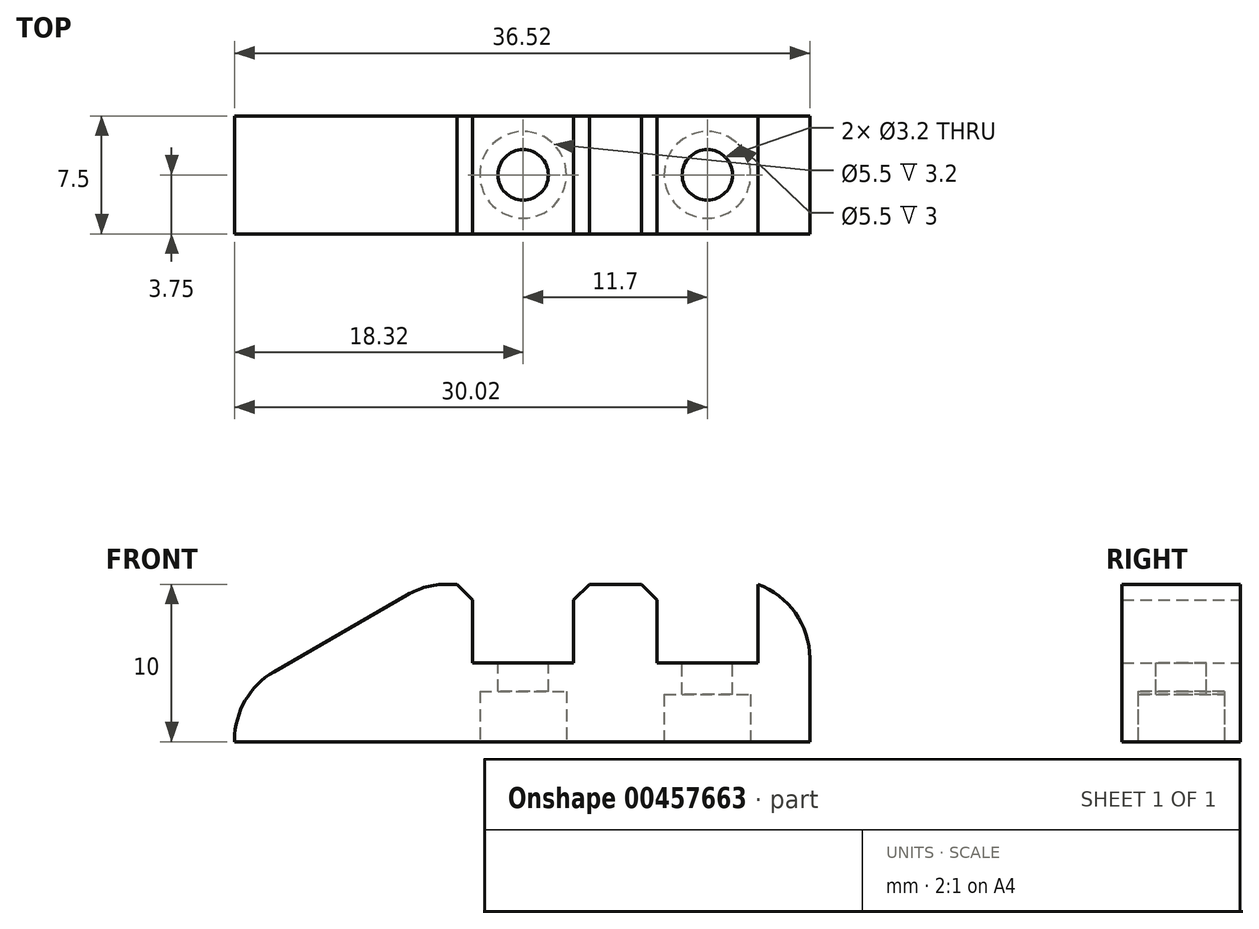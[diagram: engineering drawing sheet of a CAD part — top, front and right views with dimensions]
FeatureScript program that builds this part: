
annotation { "Feature Type Name" : "Feature", "Feature Type Description" : "" }
export const myFeature = defineFeature(function(context is Context, id is Id, definition is map)
    precondition{}
    {
        {
            var Q0;
            Q0=qCreatedBy(makeId("Front.planeOp"),FACE);
            var sketch = newSketch(context, id + "F0", { "sketchPlane" : qUnion([Q0])});
            skLineSegment(sketch, "E0", {"start": v(0, 0) * mm, "end": v(0, 10) * mm});
            skLineSegment(sketch, "E1", {"start": v(0, 10) * mm, "end": v(-3, 10) * mm});
            skLineSegment(sketch, "E2", {"start": v(-3, 10) * mm, "end": v(-3, 5) * mm});
            skLineSegment(sketch, "E3", {"start": v(-3, 5) * mm, "end": v(-9.4, 5) * mm});
            skLineSegment(sketch, "E4", {"start": v(-9.4, 5) * mm, "end": v(-9.4, 10) * mm});
            skLineSegment(sketch, "E5", {"start": v(-9.4, 10) * mm, "end": v(-12.4, 10) * mm});
            skLineSegment(sketch, "E6", {"start": v(-12.4, 10) * mm, "end": v(-24.52, 3) * mm});
            skLineSegment(sketch, "E7", {"start": v(-24.52, 3) * mm, "end": v(-24.52, 0) * mm});
            skLineSegment(sketch, "E8", {"start": v(-24.52, 0) * mm, "end": v(0, 0) * mm});
            skSolve(sketch);
        }
        {
            var Q0;
            Q0=makeQuery(id+"F0.imprint","IMPRINT",FACE,{"disambiguationData":[TD([[makeQuery(id+"F0.imprint","IMPRINT",EDGE,{"derivedFrom":sQuery(id+"F0.wireOp",EDGE,"E0")}),1.0]])]});
            extrude(context, id + "F1", {"entities" : qUnion([Q0]), "depth" : 7.5 * mm});
        }
        {
            var Q0;
            Q0=makeQuery(id+"F1.opExtrude","SWEPT_FACE",FACE,{"disambiguationData":[OSD([sQuery(id+"F0.wireOp",EDGE,"E3")])]});
            var sketch = newSketch(context, id + "F2", { "sketchPlane" : qUnion([Q0])});
            skCircle(sketch, "E9", {"center": v(-6.2, -3.75) * mm, "radius": 1.6 * mm});
            skSolve(sketch);
        }
        {
            var Q0;
            Q0=makeQuery(id+"F2.imprint","IMPRINT",FACE,{"disambiguationData":[TD([[makeQuery(id+"F2.imprint","IMPRINT",EDGE,{"derivedFrom":sQuery(id+"F2.wireOp",EDGE,"E9")}),1.0]])]});
            extrude(context, id + "F3", {"entities" : qUnion([Q0]), "operationType" : NewBodyOperationType.REMOVE, "endBound" : BoundingType.THROUGH_ALL, "oppositeDirection" : true, "depth" : 25 * mm});
        }
        {
            var Q0;
            Q0=makeQuery(id+"F1.opExtrude","SWEPT_FACE",FACE,{"disambiguationData":[OSD([sQuery(id+"F0.wireOp",EDGE,"E8")])]});
            var sketch = newSketch(context, id + "F4", { "sketchPlane" : qUnion([Q0])});
            skCircle(sketch, "E10", {"center": v(-6.2, 3.75) * mm, "radius": 2.75 * mm});
            skSolve(sketch);
        }
        {
            var Q0;
            Q0=makeQuery(id+"F4.imprint","IMPRINT",FACE,{"disambiguationData":[TD([[makeQuery(id+"F4.imprint","IMPRINT",EDGE,{"derivedFrom":sQuery(id+"F4.wireOp",EDGE,"E10")}),1.0]])]});
            extrude(context, id + "F5", {"entities" : qUnion([Q0]), "operationType" : NewBodyOperationType.REMOVE, "oppositeDirection" : true, "depth" : 3.2 * mm});
        }
        {
            var Q0;
            Q0=makeQuery(id+"F1.opExtrude","SWEPT_EDGE",EDGE,{"disambiguationData":[OSD([sQuery(id+"F0.wireOp",EDGE,"E5"),sQuery(id+"F0.wireOp",EDGE,"E6")])]});
            var Q1;
            Q1=makeQuery(id+"F1.opExtrude","SWEPT_EDGE",EDGE,{"disambiguationData":[OSD([sQuery(id+"F0.wireOp",EDGE,"E6"),sQuery(id+"F0.wireOp",EDGE,"E7")])]});
            fillet(context, id + "F6", {"entities" : qUnion([Q0, Q1]), "radius" : 5 * mm, "tangentPropagation" : true, "allowEdgeOverflow" : false});
        }
        {
            var Q0;
            Q0=makeQuery(id+"F2dZ7Sqy7HbEyPQ_1.opFillet","BLEND_EDGE",EDGE,{"blendedFrom":[makeQuery(id+"F1.opExtrude","SWEPT_EDGE",EDGE,{"disambiguationData":[OSD([sQuery(id+"F0.wireOp",EDGE,"E0"),sQuery(id+"F0.wireOp",EDGE,"E1")])]}),makeQuery(id+"F1.opExtrude","SWEPT_FACE",FACE,{"disambiguationData":[OSD([sQuery(id+"F0.wireOp",EDGE,"E2")])]})],"blendedInto":[makeQuery(id+"F1.opExtrude","SWEPT_FACE",FACE,{"disambiguationData":[OSD([sQuery(id+"F0.wireOp",EDGE,"E2")])]})]});
            var Q1;
            Q1=makeQuery(id+"F1.opExtrude","SWEPT_EDGE",EDGE,{"disambiguationData":[OSD([sQuery(id+"F0.wireOp",EDGE,"E4"),sQuery(id+"F0.wireOp",EDGE,"E5")])]});
            chamfer(context, id + "F7", {"entities" : qUnion([Q0, Q1]), "width" : 1 * mm, "tangentPropagation" : true});
        }
        {
            var Q0;
            Q0=makeQuery(id+"F1.opExtrude","SWEPT_FACE",FACE,{"disambiguationData":[OSD([sQuery(id+"F0.wireOp",EDGE,"E0")])]});
            extrude(context, id + "F8", {"entities" : qUnion([Q0]), "operationType" : NewBodyOperationType.ADD, "depth" : 12 * mm});
        }
        {
            var Q0;
            {var subQ0=sQuery(id+"F0.wireOp",EDGE,"E0");Q0=makeQuery(id+"F8.boolean.opBoolean","MERGE",FACE,{"derivedFrom":[makeQuery(id+"F1.opExtrude","CAP_FACE",FACE,{"disambiguationData":[OSD([subQ0,sQuery(id+"F0.wireOp",EDGE,"E1"),sQuery(id+"F0.wireOp",EDGE,"E2"),sQuery(id+"F0.wireOp",EDGE,"E3"),sQuery(id+"F0.wireOp",EDGE,"E4"),sQuery(id+"F0.wireOp",EDGE,"E5"),sQuery(id+"F0.wireOp",EDGE,"E6"),sQuery(id+"F0.wireOp",EDGE,"E7"),sQuery(id+"F0.wireOp",EDGE,"E8")])],"isStart":false}),makeQuery(id+"F8.opExtrude","SWEPT_FACE",FACE,{"disambiguationData":[OSD([subQ0]),TDD([makeQuery(id+"F1.opExtrude","CAP_EDGE",EDGE,{"disambiguationData":[OSD([subQ0])],"isStart":false})])]})]});}
            var sketch = newSketch(context, id + "F9", { "sketchPlane" : qUnion([Q0])});
            skLineSegment(sketch, "E11.bottom", {"start": v(2.3, 10) * mm, "end": v(8.7, 10) * mm});
            skLineSegment(sketch, "E11.top", {"start": v(2.3, 5) * mm, "end": v(8.7, 5) * mm});
            skLineSegment(sketch, "E11.left", {"start": v(2.3, 10) * mm, "end": v(2.3, 5) * mm});
            skLineSegment(sketch, "E11.right", {"start": v(8.7, 10) * mm, "end": v(8.7, 5) * mm});
            skSolve(sketch);
        }
        {
            var Q0;
            Q0=makeQuery(id+"F9.imprint","IMPRINT",FACE,{"disambiguationData":[TD([[makeQuery(id+"F9.imprint","IMPRINT",EDGE,{"derivedFrom":sQuery(id+"F9.wireOp",EDGE,"E11.bottom")}),1.0]])]});
            extrude(context, id + "F10", {"entities" : qUnion([Q0]), "operationType" : NewBodyOperationType.REMOVE, "endBound" : BoundingType.THROUGH_ALL, "oppositeDirection" : true, "depth" : 25 * mm});
        }
        {
            var Q0;
            Q0=makeQuery(id+"F1.opExtrude","SWEPT_EDGE",EDGE,{"disambiguationData":[OSD([sQuery(id+"F0.wireOp",EDGE,"E1"),sQuery(id+"F0.wireOp",EDGE,"E2")])]});
            var Q1;
            Q1=makeQuery(id+"F10.boolean.opBoolean","COPY",EDGE,{"derivedFrom":makeQuery(id+"F10.opExtrude","SWEPT_EDGE",EDGE,{"disambiguationData":[OSD([sQuery(id+"F0.wireOp",EDGE,"E0"),sQuery(id+"F0.wireOp",EDGE,"E1"),sQuery(id+"F9.wireOp",EDGE,"E11.bottom"),sQuery(id+"F9.wireOp",EDGE,"E11.left")])]})});
            var Q2;
            Q2=makeQuery(id+"F10.boolean.opBoolean","COPY",EDGE,{"derivedFrom":makeQuery(id+"F10.opExtrude","SWEPT_EDGE",EDGE,{"disambiguationData":[OSD([sQuery(id+"F0.wireOp",EDGE,"E0"),sQuery(id+"F0.wireOp",EDGE,"E1"),sQuery(id+"F9.wireOp",EDGE,"E11.bottom"),sQuery(id+"F9.wireOp",EDGE,"E11.right")])]})});
            chamfer(context, id + "F11", {"entities" : qUnion([Q0, Q1, Q2]), "width" : 1 * mm, "tangentPropagation" : true});
        }
        {
            var Q0;
            Q0=makeQuery(id+"F8.opExtrude","CAP_EDGE",EDGE,{"disambiguationData":[OSD([sQuery(id+"F0.wireOp",EDGE,"E0"),sQuery(id+"F0.wireOp",EDGE,"E1")])],"isStart":false});
            fillet(context, id + "F12", {"entities" : qUnion([Q0]), "radius" : 5 * mm, "tangentPropagation" : true, "allowEdgeOverflow" : false});
        }
        {
            var Q0;
            Q0=makeQuery(id+"F10.boolean.opBoolean","COPY",FACE,{"derivedFrom":makeQuery(id+"F10.opExtrude","SWEPT_FACE",FACE,{"disambiguationData":[OSD([sQuery(id+"F9.wireOp",EDGE,"E11.top")])]})});
            var sketch = newSketch(context, id + "F13", { "sketchPlane" : qUnion([Q0])});
            skCircle(sketch, "E12", {"center": v(5.5, -3.75) * mm, "radius": 1.6 * mm});
            skSolve(sketch);
        }
        {
            var Q0;
            Q0=makeQuery(id+"F13.imprint","IMPRINT",FACE,{"disambiguationData":[TD([[makeQuery(id+"F13.imprint","IMPRINT",EDGE,{"derivedFrom":sQuery(id+"F13.wireOp",EDGE,"E12")}),1.0]])]});
            extrude(context, id + "F14", {"entities" : qUnion([Q0]), "operationType" : NewBodyOperationType.REMOVE, "endBound" : BoundingType.THROUGH_ALL, "oppositeDirection" : true, "depth" : 25 * mm});
        }
        {
            var Q0;
            {var subQ0=sQuery(id+"F0.wireOp",EDGE,"E8");Q0=makeQuery(id+"F8.boolean.opBoolean","MERGE",FACE,{"derivedFrom":[makeQuery(id+"F1.opExtrude","SWEPT_FACE",FACE,{"disambiguationData":[OSD([subQ0])]}),makeQuery(id+"F8.opExtrude","SWEPT_FACE",FACE,{"disambiguationData":[OSD([sQuery(id+"F0.wireOp",EDGE,"E0"),subQ0])]})]});}
            var sketch = newSketch(context, id + "F15", { "sketchPlane" : qUnion([Q0])});
            skCircle(sketch, "E13", {"center": v(5.5, 3.75) * mm, "radius": 2.75 * mm});
            skSolve(sketch);
        }
        {
            var Q0;
            Q0=makeQuery(id+"F15.imprint","IMPRINT",FACE,{"disambiguationData":[TD([[makeQuery(id+"F15.imprint","IMPRINT",EDGE,{"derivedFrom":sQuery(id+"F15.wireOp",EDGE,"E13")}),1.0]])]});
            extrude(context, id + "F16", {"entities" : qUnion([Q0]), "operationType" : NewBodyOperationType.REMOVE, "oppositeDirection" : true, "depth" : 3 * mm});
        }
    });
